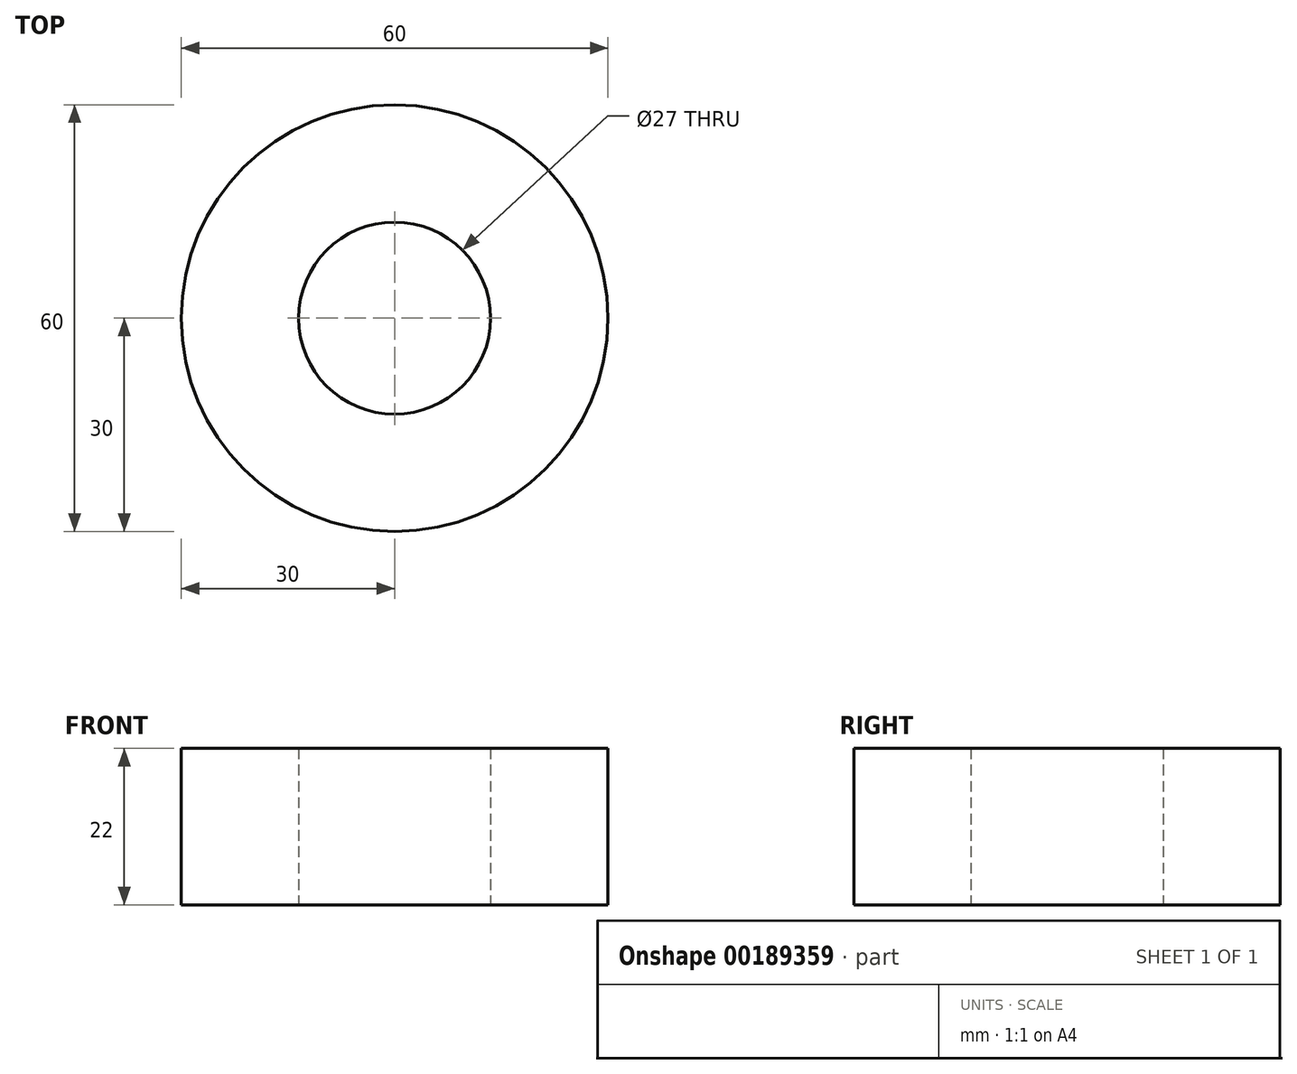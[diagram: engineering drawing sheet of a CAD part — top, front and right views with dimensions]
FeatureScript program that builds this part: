
annotation { "Feature Type Name" : "Feature", "Feature Type Description" : "" }
export const myFeature = defineFeature(function(context is Context, id is Id, definition is map)
    precondition{}
    {
        {
            var Q0;
            Q0=qCreatedBy(makeId("Top.planeOp"),FACE);
            var sketch = newSketch(context, id + "F0", { "sketchPlane" : qUnion([Q0])});
            skCircle(sketch, "E0", {"center": v(0, 0) * mm, "radius": 13.5 * mm});
            skCircle(sketch, "E1", {"center": v(0, 0) * mm, "radius": 30 * mm});
            skSolve(sketch);
        }
        {
            var Q0;
            Q0 = qSketchRegion(id + "F0", true);
            extrude(context, id + "F1", {"entities" : qUnion([Q0]), "depth" : 22 * mm});
        }
    });
